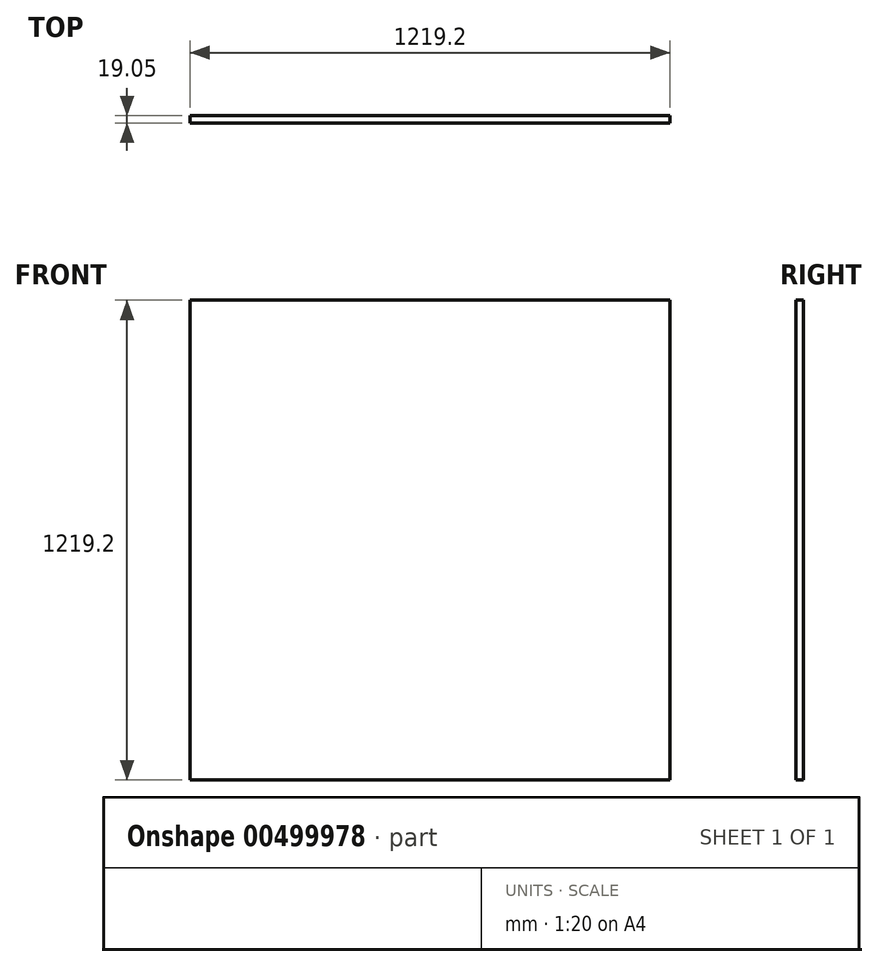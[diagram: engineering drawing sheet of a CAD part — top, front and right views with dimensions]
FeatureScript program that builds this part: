
annotation { "Feature Type Name" : "Feature", "Feature Type Description" : "" }
export const myFeature = defineFeature(function(context is Context, id is Id, definition is map)
    precondition{}
    {
        {
            var Q0;
            Q0=qCreatedBy(makeId("Front.planeOp"),FACE);
            var sketch = newSketch(context, id + "F0", { "sketchPlane" : qUnion([Q0])});
            skLineSegment(sketch, "E0.bottom", {"start": v(-609.6, 609.6) * mm, "end": v(609.6, 609.6) * mm});
            skLineSegment(sketch, "E0.top", {"start": v(-609.6, -609.6) * mm, "end": v(609.6, -609.6) * mm});
            skLineSegment(sketch, "E0.left", {"start": v(-609.6, 609.6) * mm, "end": v(-609.6, -609.6) * mm});
            skLineSegment(sketch, "E0.right", {"start": v(609.6, 609.6) * mm, "end": v(609.6, -609.6) * mm});
            skPoint(sketch, "E0.middle", {"position": v(0, 0) * mm});
            skSolve(sketch);
        }
        {
            var Q0;
            Q0=makeQuery(id+"F0.imprint","IMPRINT",FACE,{"disambiguationData":[TD([[makeQuery(id+"F0.imprint","IMPRINT",EDGE,{"derivedFrom":sQuery(id+"F0.wireOp",EDGE,"E0.bottom")}),-1.0]])]});
            var Q1;
            Q1=makeQuery(id+"F0.imprint","IMPRINT",FACE,{"disambiguationData":[TD([[makeQuery(id+"F0.imprint","IMPRINT",EDGE,{"derivedFrom":sQuery(id+"F0.wireOp",EDGE,"E0.bottom")}),1.0]])]});
            var Q2;
            {var subQ0=sQuery(id+"F0.wireOp",EDGE,"6VFQsjTd-rd8c-a5bZ-oaXC-JIrlvXfZp1Mn");Q2=makeQuery(id+"F0.imprint","IMPRINT",FACE,{"disambiguationData":[TD([[makeQuery(id+"F0.imprint","IMPRINT",EDGE,{"derivedFrom":subQ0}),-1.0]])]});}
            extrude(context, id + "F1", {"entities" : qUnion([Q0, Q1, Q2]), "depth" : 19.05 * mm, "offsetDistance" : 25.4 * mm});
        }
    });
